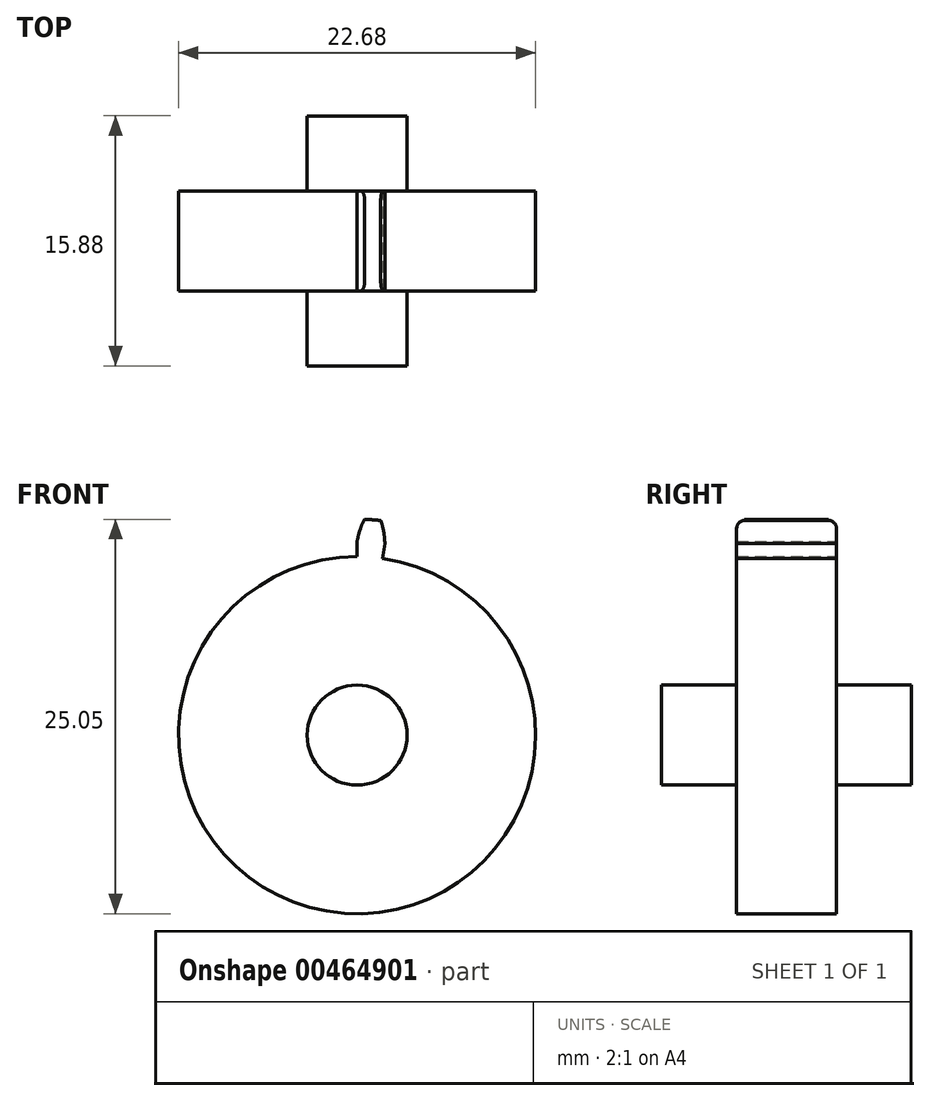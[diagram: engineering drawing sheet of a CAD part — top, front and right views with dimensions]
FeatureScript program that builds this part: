
annotation { "Feature Type Name" : "Feature", "Feature Type Description" : "" }
export const myFeature = defineFeature(function(context is Context, id is Id, definition is map)
    precondition{}
    {
        {
            var Q0;
            Q0=qCreatedBy(makeId("Front.planeOp"),FACE);
            var sketch = newSketch(context, id + "F0", { "sketchPlane" : qUnion([Q0])});
            skCircle(sketch, "E0", {"center": v(0, 0) * mm, "radius": 11.34 * mm});
            skSolve(sketch);
        }
        {
            var Q0;
            Q0=makeQuery(id+"F0.imprint","IMPRINT",FACE,{"disambiguationData":[TD([[makeQuery(id+"F0.imprint","IMPRINT",EDGE,{"derivedFrom":sQuery(id+"F0.wireOp",EDGE,"E0")}),1.0]])]});
            extrude(context, id + "F1", {"entities" : qUnion([Q0]), "endBound" : BoundingType.SYMMETRIC, "depth" : 6.35 * mm});
        }
        {
            var Q0;
            Q0=qCreatedBy(makeId("Front.planeOp"),FACE);
            var sketch = newSketch(context, id + "F2", { "sketchPlane" : qUnion([Q0])});
            skCircle(sketch, "E1", {"center": v(0, 0) * mm, "radius": 3.18 * mm});
            skSolve(sketch);
        }
        {
            var Q0;
            Q0 = qSketchRegion(id + "F2", true);
            extrude(context, id + "F3", {"entities" : qUnion([Q0]), "operationType" : NewBodyOperationType.ADD, "endBound" : BoundingType.SYMMETRIC, "depth" : 15.88 * mm});
        }
        {
            var Q0;
            Q0=qCreatedBy(makeId("Front.planeOp"),FACE);
            var sketch = newSketch(context, id + "F4", { "sketchPlane" : qUnion([Q0])});
            skLineSegment(sketch, "E2", {"start": v(0, 0) * mm, "end": v(0, 19.2) * mm, "construction": true});
            skLineSegment(sketch, "E3", {"start": v(0, 0) * mm, "end": v(2.75, 19) * mm, "construction": true});
            skPoint(sketch, "E4.center", {"position": v(0, 0) * mm});
            skLineSegment(sketch, "E5", {"start": v(0, 0) * mm, "end": v(1.37, 19.07) * mm, "construction": true});
            skLineSegment(sketch, "E6", {"start": v(0, 0) * mm, "end": v(0.66, 19.43) * mm, "construction": true});
            skLineSegment(sketch, "E7", {"start": v(0, 0) * mm, "end": v(2.13, 19.3) * mm, "construction": true});
            skCircle(sketch, "E8", {"center": v(0, 0) * mm, "radius": 13.72 * mm, "construction": true});
            skCircle(sketch, "E9", {"center": v(0, 0) * mm, "radius": 12.3 * mm, "construction": true});
            skLineSegment(sketch, "E10", {"start": v(1.63, 11.22) * mm, "end": v(1.76, 12.17) * mm});
            skLineSegment(sketch, "E11", {"start": v(0, 12.3) * mm, "end": v(0, 11.34) * mm});
            skArc(sketch, "E12", {"start": v(0.47, 13.7) * mm, "mid": v(0.18, 13.02) * mm, "end": v(0, 12.3) * mm});
            skArc(sketch, "E13", {"start": v(1.76, 12.17) * mm, "mid": v(1.7, 12.91) * mm, "end": v(1.5, 13.63) * mm});
            skArc(sketch, "E14", {"start": v(1.5, 13.63) * mm, "mid": v(0.99, 13.68) * mm, "end": v(0.47, 13.7) * mm});
            skArc(sketch, "E15", {"start": v(1.63, 11.22) * mm, "mid": v(0.81, 11.31) * mm, "end": v(0, 11.34) * mm});
            skSolve(sketch);
        }
        {
            var Q0;
            Q0 = qSketchRegion(id + "F4", true);
            extrude(context, id + "F5", {"entities" : qUnion([Q0]), "operationType" : NewBodyOperationType.ADD, "endBound" : BoundingType.SYMMETRIC, "depth" : 6.35 * mm});
        }
        {
            var Q0;
            Q0=makeQuery(id+"F5.opExtrude","SWEPT_EDGE",EDGE,{"disambiguationData":[OSD([sQuery(id+"F4.wireOp",EDGE,"E10"),sQuery(id+"F4.wireOp",EDGE,"E15")])]});
            var Q1;
            Q1=makeQuery(id+"F4kfKp8FkYmbN8U_1.1.F5.opExtrude","SWEPT_EDGE",EDGE,{"disambiguationData":[OSD([sQuery(id+"F4.wireOp",EDGE,"E11"),sQuery(id+"F4.wireOp",EDGE,"E15")])]});
            var Q2;
            Q2=makeQuery(id+"F5.opExtrude","SWEPT_EDGE",EDGE,{"disambiguationData":[OSD([sQuery(id+"F4.wireOp",EDGE,"E11"),sQuery(id+"F4.wireOp",EDGE,"E15")])]});
            var Q3;
            Q3=makeQuery(id+"F4kfKp8FkYmbN8U_1.23.F5.opExtrude","SWEPT_EDGE",EDGE,{"disambiguationData":[OSD([sQuery(id+"F4.wireOp",EDGE,"E10"),sQuery(id+"F4.wireOp",EDGE,"E15")])]});
            var Q4;
            Q4=makeQuery(id+"F5.opExtrude","CAP_EDGE",EDGE,{"disambiguationData":[OSD([sQuery(id+"F4.wireOp",EDGE,"E14")])],"isStart":false});
            var Q5;
            Q5=makeQuery(id+"F4kfKp8FkYmbN8U_1.1.F5.opExtrude","CAP_EDGE",EDGE,{"disambiguationData":[OSD([sQuery(id+"F4.wireOp",EDGE,"E14")])],"isStart":false});
            var Q6;
            Q6=makeQuery(id+"F4kfKp8FkYmbN8U_1.23.F5.opExtrude","CAP_EDGE",EDGE,{"disambiguationData":[OSD([sQuery(id+"F4.wireOp",EDGE,"E14")])],"isStart":false});
            var Q7;
            Q7=makeQuery(id+"F4kfKp8FkYmbN8U_1.23.F5.opExtrude","CAP_EDGE",EDGE,{"disambiguationData":[OSD([sQuery(id+"F4.wireOp",EDGE,"E14")])],"isStart":true});
            var Q8;
            Q8=makeQuery(id+"F5.opExtrude","CAP_EDGE",EDGE,{"disambiguationData":[OSD([sQuery(id+"F4.wireOp",EDGE,"E14")])],"isStart":true});
            var Q9;
            Q9=makeQuery(id+"F4kfKp8FkYmbN8U_1.1.F5.opExtrude","CAP_EDGE",EDGE,{"disambiguationData":[OSD([sQuery(id+"F4.wireOp",EDGE,"E14")])],"isStart":true});
            fillet(context, id + "F6", {"entities" : qUnion([Q0, Q1, Q2, Q3, Q4, Q5, Q6, Q7, Q8, Q9]), "radius" : 0.5 * mm, "tangentPropagation" : true, "allowEdgeOverflow" : false});
        }
    });
